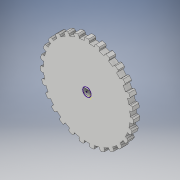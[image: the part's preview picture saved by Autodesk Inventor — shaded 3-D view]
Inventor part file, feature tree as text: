
AUTODESK INVENTOR PART (.ipt)
format: ipt  version: 2017 (Build 210142000, 142)  size: 323,584 bytes
history: native  units: in
note: dims shown in document units (in); Inventor stores cm internally (conversion verified against a paired STEP export)
features: sketch x3, extrude x2, pattern_circular x1
ambient origin geometry x8: Origin, YZ Plane, XZ Plane, XY Plane, X Axis, Y Axis, Z Axis, Center Point
bodies: Solid1 (feature_tree)
feature tree (6):
  extrude  "Extrusion1"  Depth=0.075in
  pattern_circular  "Circular Pattern1"  Count=108 Angle=360.0deg
  extrude  "Extrusion2"  Depth=0.062in
  sketch  "Sketch3"  dims[d6=0.04in d7=42.5197in d9=360.0deg d11=0.062in d12=0.062in d13=0.15in d14=0.0in d15=10.6299in d16=360.0deg d18=0.0591in d19=0.15in d20=0.0in]
  sketch  "Sketch1"  dims[d0=2.025in d4=0.075in]
  sketch  "Sketch2"  dims[d5=0.04in]
